# Revit family: 50290_BEGA_Revit
name_source: partatom
category: Lighting Fixtures
revit_build: Autodesk Revit LT 2017 (Build: 20160225_1515(x64)
units: mm (PartAtom-declared; Revit-internal decimal feet)

## family parameters
Cut with Voids When Loaded = Yes
Host = Face
Light Source = Yes
Part Type = Normal
Room Calculation Point = No
Round Connector Dimension = Use Diameter
Shared = No

## types (4) — shared parameters
Color Filter = 16777215
Default Elevation = 6' - 0"
Dimming Lamp Color Temperature Shift = <None>
Manufacturer = BEGA-US
Telephone = 805.684.0533
URL = www.bega-us.com

## per-type parameters (varying)
| type | Description | Lamp | Model | Photometric Web File | Tilt Angle |
| Wall Luminaires - Directed Light | Surface wall with cutoff optics | 44.6W LED | 2260LED | generic | 90.00° |
| Wall Luminaires - Linear | Suface wall - linear with white acrylic diffuser | (1) 39W CF twin-4-p | 4425P | generic | 90.00° |
| Ceiling and Wall Luminaires - Unshielded | LED ceiling and wall luminaires - impact resistant | 8.4W LED | 33 508 | 50290K65_BEGA_IES.ies | 180.00° |
| Recessed Ceiling and wall luminaires | Recessed Ceiling and wall luminaires | 8.4W LED | 50 290 | 50290K65_BEGA_IES.ies | 180.00° |

## geometry (parser evidence)
native form markers: Blend x21, Sweep x6
no freeform markers — native parametric forms only
